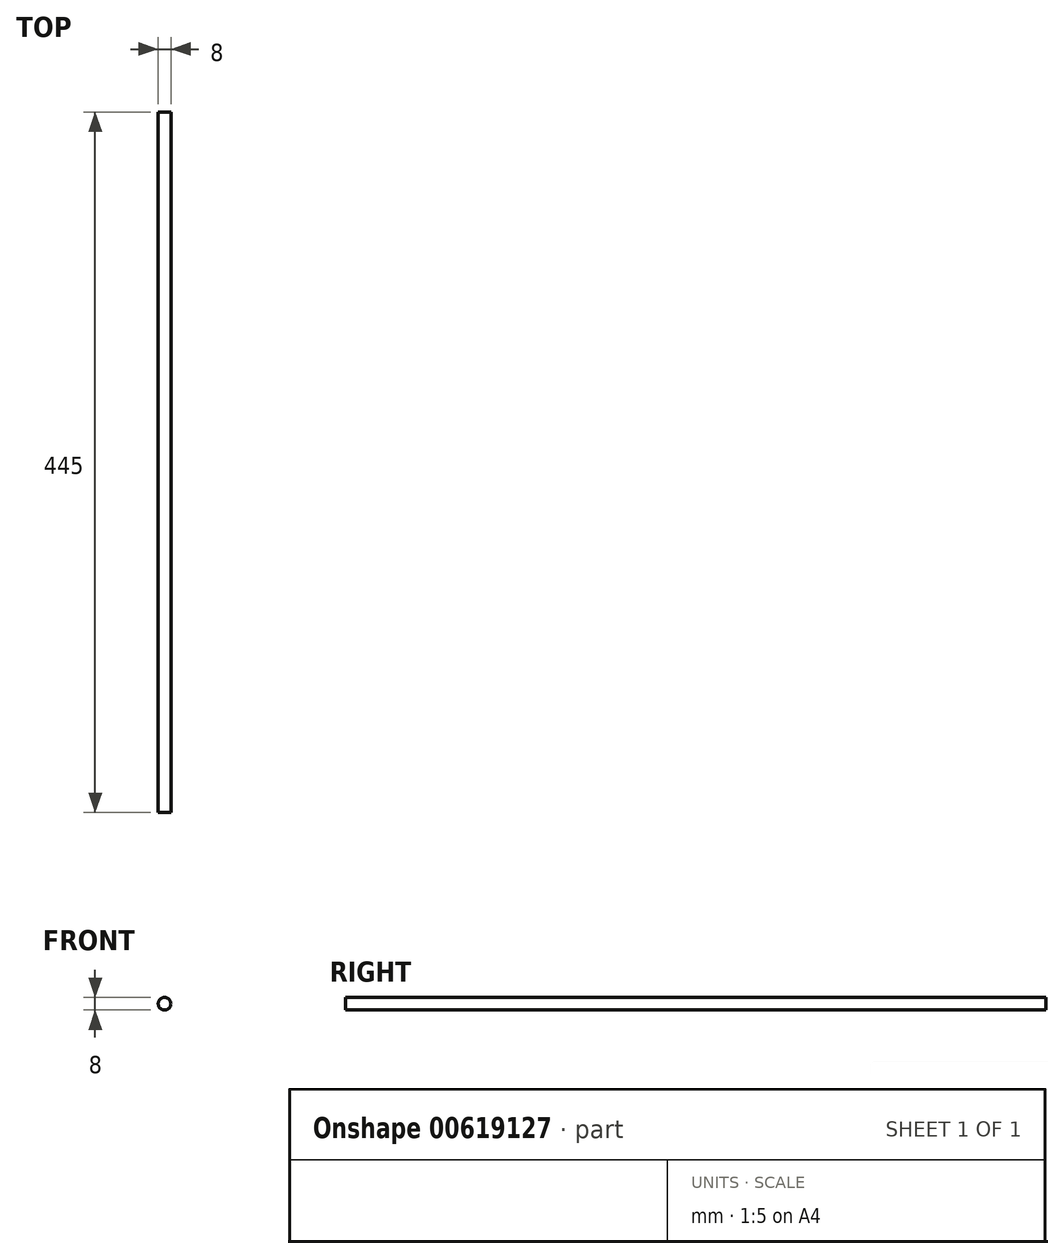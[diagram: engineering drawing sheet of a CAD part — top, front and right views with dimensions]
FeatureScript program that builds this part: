
annotation { "Feature Type Name" : "Feature", "Feature Type Description" : "" }
export const myFeature = defineFeature(function(context is Context, id is Id, definition is map)
    precondition{}
    {
        {
            var Q0;
            Q0=qCreatedBy(makeId("Front.planeOp"),FACE);
            var sketch = newSketch(context, id + "F0", { "sketchPlane" : qUnion([Q0])});
            skCircle(sketch, "E0", {"center": v(0, 0) * mm, "radius": 4 * mm});
            skSolve(sketch);
        }
        {
            var Q0;
            Q0=qSketchRegion(id+"F0",true);
            extrude(context, id + "F1", {"entities" : qUnion([Q0]), "depth" : 445 * mm, "offsetDistance" : 25 * mm});
        }
    });
